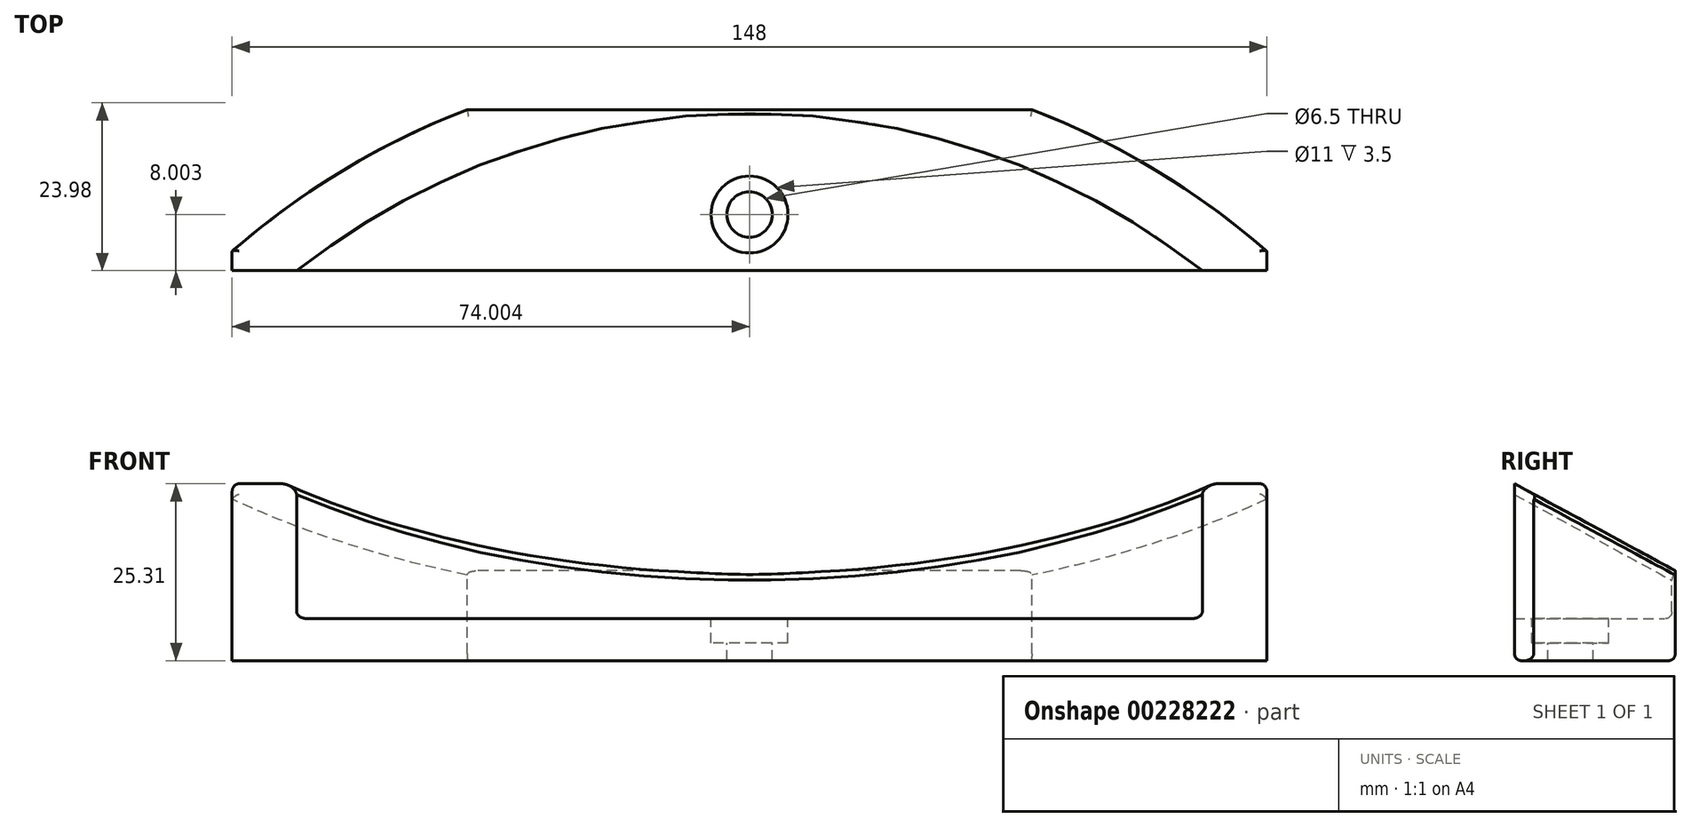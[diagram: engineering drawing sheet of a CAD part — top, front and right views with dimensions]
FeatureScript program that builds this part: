
annotation { "Feature Type Name" : "Feature", "Feature Type Description" : "" }
export const myFeature = defineFeature(function(context is Context, id is Id, definition is map)
    precondition{}
    {
        {
            var Q0;
            Q0=qCreatedBy(makeId("Top.planeOp"),FACE);
            var sketch = newSketch(context, id + "F0", { "sketchPlane" : qUnion([Q0])});
            skLineSegment(sketch, "E0.bottom", {"start": v(-72.48, -7.14) * mm, "end": v(107.52, -7.14) * mm});
            skLineSegment(sketch, "E0.top", {"start": v(-72.48, -30.14) * mm, "end": v(107.52, -30.14) * mm});
            skLineSegment(sketch, "E0.left", {"start": v(-72.48, -7.14) * mm, "end": v(-72.48, -30.14) * mm});
            skLineSegment(sketch, "E0.right", {"start": v(107.52, -7.14) * mm, "end": v(107.52, -30.14) * mm});
            skPoint(sketch, "E1", {"position": v(-64.48, -22.14) * mm});
            skPoint(sketch, "E2", {"position": v(99.52, -22.14) * mm});
            skSolve(sketch);
        }
        {
            var Q0;
            Q0=makeQuery(id+"F0.imprint","IMPRINT",FACE,{"disambiguationData":[TD([[makeQuery(id+"F0.imprint","IMPRINT",EDGE,{"derivedFrom":sQuery(id+"F0.wireOp",EDGE,"E0.bottom")}),-1.0]])]});
            extrude(context, id + "F1", {"entities" : qUnion([Q0]), "depth" : 6 * mm});
        }
        {
            var Q0;
            Q0=makeQuery(id+"F1.opExtrude","CAP_FACE",FACE,{"disambiguationData":[OSD([sQuery(id+"F0.wireOp",EDGE,"E0.bottom"),sQuery(id+"F0.wireOp",EDGE,"E0.top"),sQuery(id+"F0.wireOp",EDGE,"E0.left"),sQuery(id+"F0.wireOp",EDGE,"E0.right")])],"isStart":false});
            var sketch = newSketch(context, id + "F2", { "sketchPlane" : qUnion([Q0])});
            skPoint(sketch, "E3", {"position": v(-64.48, -22.14) * mm});
            skPoint(sketch, "E4", {"position": v(99.52, -22.14) * mm});
            skLineSegment(sketch, "E5.bottom", {"start": v(-56.48, -7.14) * mm, "end": v(91.52, -7.14) * mm});
            skLineSegment(sketch, "E5.top", {"start": v(-56.48, -30.14) * mm, "end": v(91.52, -30.14) * mm});
            skLineSegment(sketch, "E5.left", {"start": v(-56.48, -7.14) * mm, "end": v(-56.48, -30.14) * mm});
            skLineSegment(sketch, "E5.right", {"start": v(91.52, -7.14) * mm, "end": v(91.52, -30.14) * mm});
            skSolve(sketch);
        }
        {
            var Q0;
            Q0=makeQuery(id+"F2.imprint","IMPRINT",FACE,{"disambiguationData":[TD([[makeQuery(id+"F2.imprint","IMPRINT",EDGE,{"derivedFrom":sQuery(id+"F2.wireOp",EDGE,"E5.bottom")}),-1.0]])]});
            extrude(context, id + "F3", {"entities" : qUnion([Q0]), "operationType" : NewBodyOperationType.ADD, "depth" : 21 * mm});
        }
        {
            var Q0;
            Q0=makeQuery(id+"F3.opExtrude","CAP_FACE",FACE,{"disambiguationData":[OSD([sQuery(id+"F2.wireOp",EDGE,"E5.bottom"),sQuery(id+"F2.wireOp",EDGE,"E5.top"),sQuery(id+"F2.wireOp",EDGE,"E5.left"),sQuery(id+"F2.wireOp",EDGE,"E5.right")])],"isStart":false});
            var sketch = newSketch(context, id + "F4", { "sketchPlane" : qUnion([Q0])});
            skPoint(sketch, "E6", {"position": v(17.52, 2.86) * mm});
            skCircle(sketch, "E7", {"center": v(17.52, -112.14) * mm, "radius": 112.5 * mm});
            skCircle(sketch, "E8", {"center": v(17.52, -112.14) * mm, "radius": 104.5 * mm});
            skSolve(sketch);
        }
        {
            var Q0;
            {var subQ0=sQuery(id+"F4.wireOp",EDGE,"E8");var subQ1=makeQuery(id+"F3.opExtrude","CAP_EDGE",EDGE,{"disambiguationData":[OSD([sQuery(id+"F2.wireOp",EDGE,"E5.top")])],"isStart":false});var subQ2=makeQuery(id+"F4.imprint","INTERSECT",VERTEX,{"disambiguationData":[OD(0.0)],"derivedFrom":[subQ1,subQ0]});Q0=makeQuery(id+"F4.imprint","IMPRINT",FACE,{"disambiguationData":[TD([[makeQuery(id+"F4.imprint","IMPRINT",EDGE,{"disambiguationData":[TD([[subQ2,1.0]])],"derivedFrom":subQ0}),1.0]])]});}
            extrude(context, id + "F5", {"entities" : qUnion([Q0]), "operationType" : NewBodyOperationType.REMOVE, "oppositeDirection" : true, "depth" : 21 * mm});
        }
        {
            var Q0;
            {var subQ0=sQuery(id+"F4.wireOp",EDGE,"E7");var subQ1=makeQuery(id+"F3.opExtrude","CAP_EDGE",EDGE,{"disambiguationData":[OSD([sQuery(id+"F2.wireOp",EDGE,"E5.bottom")])],"isStart":false});var subQ2=makeQuery(id+"F4.imprint","INTERSECT",VERTEX,{"disambiguationData":[OD(1.0)],"derivedFrom":[subQ1,subQ0]});Q0=makeQuery(id+"F4.imprint","IMPRINT",FACE,{"disambiguationData":[TD([[makeQuery(id+"F4.imprint","IMPRINT",EDGE,{"disambiguationData":[TD([[subQ2,-1.0]])],"derivedFrom":subQ0}),-1.0]])]});}
            var Q1;
            {var subQ0=sQuery(id+"F4.wireOp",EDGE,"E7");var subQ1=makeQuery(id+"F3.opExtrude","CAP_EDGE",EDGE,{"disambiguationData":[OSD([sQuery(id+"F2.wireOp",EDGE,"E5.bottom")])],"isStart":false});var subQ2=makeQuery(id+"F4.imprint","INTERSECT",VERTEX,{"disambiguationData":[OD(0.0)],"derivedFrom":[subQ1,subQ0]});Q1=makeQuery(id+"F4.imprint","IMPRINT",FACE,{"disambiguationData":[TD([[makeQuery(id+"F4.imprint","IMPRINT",EDGE,{"disambiguationData":[TD([[subQ2,1.0]])],"derivedFrom":subQ0}),-1.0]])]});}
            extrude(context, id + "F6", {"entities" : qUnion([Q0, Q1]), "operationType" : NewBodyOperationType.REMOVE, "oppositeDirection" : true, "depth" : 35 * mm});
        }
        {
            var Q0;
            Q0=makeQuery(id+"F1.opExtrude","SWEPT_FACE",FACE,{"disambiguationData":[OSD([sQuery(id+"F0.wireOp",EDGE,"E0.right")])]});
            var sketch = newSketch(context, id + "F7", { "sketchPlane" : qUnion([Q0])});
            skLineSegment(sketch, "E9", {"start": v(-33.26, 27) * mm, "end": v(-1.82, 10) * mm});
            skLineSegment(sketch, "E10", {"start": v(-1.82, 10) * mm, "end": v(-1.82, 27.27) * mm});
            skLineSegment(sketch, "E11", {"start": v(-1.82, 27.27) * mm, "end": v(-33.26, 27) * mm});
            skSolve(sketch);
        }
        {
            var Q0;
            Q0=makeQuery(id+"F7.imprint","IMPRINT",FACE,{"disambiguationData":[TD([[makeQuery(id+"F7.imprint","IMPRINT",EDGE,{"derivedFrom":sQuery(id+"F7.wireOp",EDGE,"E9")}),1.0]])]});
            extrude(context, id + "F8", {"entities" : qUnion([Q0]), "operationType" : NewBodyOperationType.REMOVE, "oppositeDirection" : true, "depth" : 200 * mm});
        }
        {
            var Q0;
            {var subQ0=sQuery(id+"F2.wireOp",EDGE,"E5.left");Q0=makeQuery(id+"F2.imprint","IMPRINT",FACE,{"disambiguationData":[TD([[makeQuery(id+"F2.imprint","IMPRINT",EDGE,{"derivedFrom":subQ0}),-1.0]])]});}
            var Q1;
            {var subQ0=sQuery(id+"F2.wireOp",EDGE,"E5.right");Q1=makeQuery(id+"F2.imprint","IMPRINT",FACE,{"disambiguationData":[TD([[makeQuery(id+"F2.imprint","IMPRINT",EDGE,{"derivedFrom":subQ0}),1.0]])]});}
            extrude(context, id + "F9", {"entities" : qUnion([Q0, Q1]), "operationType" : NewBodyOperationType.REMOVE, "oppositeDirection" : true, "depth" : 25 * mm});
        }
        {
            var Q0;
            {var subQ0=sQuery(id+"F4.wireOp",EDGE,"E8");var subQ1=makeQuery(id+"F3.opExtrude","CAP_EDGE",EDGE,{"disambiguationData":[OSD([sQuery(id+"F2.wireOp",EDGE,"E5.top")])],"isStart":false});var subQ2=makeQuery(id+"F4.imprint","INTERSECT",VERTEX,{"disambiguationData":[OD(0.0)],"derivedFrom":[subQ1,subQ0]});Q0=makeQuery(id+"F4.imprint","IMPRINT",FACE,{"disambiguationData":[TD([[makeQuery(id+"F4.imprint","IMPRINT",EDGE,{"disambiguationData":[TD([[subQ2,1.0]])],"derivedFrom":subQ0}),1.0]])]});}
            var sketch = newSketch(context, id + "F10", { "sketchPlane" : qUnion([Q0])});
            skPoint(sketch, "E12", {"position": v(17.52, -22.14) * mm});
            skSolve(sketch);
        }
        {
            var Q0;
            Q0=sQuery(id+"F10.wireOp",VERTEX,"E12");
            var Q1;
            Q1=makeQuery(id+"F1.opExtrude","SWEPT_BODY",BODY,{"disambiguationData":[OSD([sQuery(id+"F0.wireOp",EDGE,"E0.bottom"),sQuery(id+"F0.wireOp",EDGE,"E0.top"),sQuery(id+"F0.wireOp",EDGE,"E0.left"),sQuery(id+"F0.wireOp",EDGE,"E0.right")])]});
            hole(context, id + "F11", {"style" : HoleStyle.C_BORE, "endStyle" : HoleEndStyle.THROUGH, "holeDiameter" : 6.5 * mm, "cBoreDiameter" : 11 * mm, "cBoreDepth" : 3.5 * mm, "locations" : qUnion([Q0]), "scope" : qUnion([Q1]), "isTappedThrough" : true});
        }
        {
            var Q0;
            Q0=makeQuery(id+"F5.boolean.opBoolean","COPY",EDGE,{"derivedFrom":makeQuery(id+"F5.opExtrude","CAP_EDGE",EDGE,{"disambiguationData":[OSD([sQuery(id+"F2.wireOp",EDGE,"E5.bottom")])],"isStart":false})});
            var Q1;
            Q1=makeQuery(id+"F5.boolean.opBoolean","COPY",EDGE,{"derivedFrom":makeQuery(id+"F5.opExtrude","CAP_EDGE",EDGE,{"disambiguationData":[OSD([sQuery(id+"F2.wireOp",EDGE,"E5.top")])],"isStart":false})});
            var Q2;
            {var subQ0=sQuery(id+"F4.wireOp",EDGE,"E7");var subQ1=sQuery(id+"F2.wireOp",EDGE,"E5.bottom");var subQ2=makeQuery(id+"F3.opExtrude","CAP_EDGE",EDGE,{"disambiguationData":[OSD([subQ1])],"isStart":false});var subQ3=sQuery(id+"F0.wireOp",EDGE,"E0.bottom");Q2=makeQuery(id+"F6.boolean.opBoolean","SPLIT",EDGE,{"disambiguationData":[TD([makeQuery(id+"F6.opExtrude","SWEPT_FACE",FACE,{"disambiguationData":[OSD([subQ0]),TDD([makeQuery(id+"F4.imprint","IMPRINT",EDGE,{"disambiguationData":[TD([[makeQuery(id+"F4.imprint","INTERSECT",VERTEX,{"disambiguationData":[OD(0.0)],"derivedFrom":[subQ2,subQ0]}),1.0]])],"derivedFrom":subQ0})])]})])],"derivedFrom":makeQuery(id+"F1.opExtrude","CAP_EDGE",EDGE,{"disambiguationData":[OSD([subQ3])],"isStart":true})});}
            var Q3;
            Q3=makeQuery(id+"F1.opExtrude","CAP_EDGE",EDGE,{"disambiguationData":[OSD([sQuery(id+"F0.wireOp",EDGE,"E0.top")])],"isStart":true});
            var Q4;
            {var subQ0=sQuery(id+"F4.wireOp",EDGE,"E7");var subQ1=sQuery(id+"F2.wireOp",EDGE,"E5.bottom");var subQ2=sQuery(id+"F2.wireOp",EDGE,"E5.left");var subQ6=sQuery(id+"F0.wireOp",EDGE,"E0.right");var subQ7=sQuery(id+"F0.wireOp",EDGE,"E0.left");var subQ8=sQuery(id+"F0.wireOp",EDGE,"E0.top");var subQ9=sQuery(id+"F0.wireOp",EDGE,"E0.bottom");var subQ11=makeQuery(id+"F6.opExtrude","SWEPT_EDGE",EDGE,{"disambiguationData":[OSD([subQ2,subQ0])]});Q4=makeQuery(id+"F9.boolean.opBoolean","MERGE",EDGE,{"derivedFrom":[makeQuery(id+"F6.boolean.opBoolean","COPY",EDGE,{"disambiguationData":[TD([makeQuery(id+"F1.opExtrude","CAP_FACE",FACE,{"disambiguationData":[OSD([subQ9,subQ8,subQ7,subQ6])],"isStart":true})])],"derivedFrom":subQ11}),makeQuery(id+"F6.boolean.opBoolean","COPY",EDGE,{"disambiguationData":[TD([makeQuery(id+"F3.opExtrude","CAP_FACE",FACE,{"disambiguationData":[OSD([subQ1,sQuery(id+"F2.wireOp",EDGE,"E5.top"),subQ2,sQuery(id+"F2.wireOp",EDGE,"E5.right")])],"isStart":false})])],"derivedFrom":subQ11})]});}
            var Q5;
            {var subQ0=sQuery(id+"F4.wireOp",EDGE,"E7");var subQ1=sQuery(id+"F2.wireOp",EDGE,"E5.bottom");Q5=makeQuery(id+"F6.boolean.opBoolean","COPY",EDGE,{"derivedFrom":makeQuery(id+"F6.opExtrude","SWEPT_EDGE",EDGE,{"disambiguationData":[OSD([subQ1,subQ0]),TDD([makeQuery(id+"F4.imprint","INTERSECT",VERTEX,{"disambiguationData":[OD(1.0)],"derivedFrom":[makeQuery(id+"F3.opExtrude","CAP_EDGE",EDGE,{"disambiguationData":[OSD([subQ1])],"isStart":false}),subQ0]})])]})});}
            var Q6;
            {var subQ0=sQuery(id+"F4.wireOp",EDGE,"E7");var subQ1=sQuery(id+"F2.wireOp",EDGE,"E5.bottom");var subQ2=sQuery(id+"F2.wireOp",EDGE,"E5.right");var subQ5=sQuery(id+"F0.wireOp",EDGE,"E0.right");var subQ6=sQuery(id+"F0.wireOp",EDGE,"E0.left");var subQ7=sQuery(id+"F0.wireOp",EDGE,"E0.top");var subQ8=sQuery(id+"F0.wireOp",EDGE,"E0.bottom");var subQ11=makeQuery(id+"F6.opExtrude","SWEPT_EDGE",EDGE,{"disambiguationData":[OSD([subQ2,subQ0])]});Q6=makeQuery(id+"F9.boolean.opBoolean","MERGE",EDGE,{"derivedFrom":[makeQuery(id+"F6.boolean.opBoolean","COPY",EDGE,{"disambiguationData":[TD([makeQuery(id+"F1.opExtrude","CAP_FACE",FACE,{"disambiguationData":[OSD([subQ8,subQ7,subQ6,subQ5])],"isStart":true})])],"derivedFrom":subQ11}),makeQuery(id+"F6.boolean.opBoolean","COPY",EDGE,{"disambiguationData":[TD([makeQuery(id+"F3.opExtrude","CAP_FACE",FACE,{"disambiguationData":[OSD([subQ1,sQuery(id+"F2.wireOp",EDGE,"E5.top"),sQuery(id+"F2.wireOp",EDGE,"E5.left"),subQ2])],"isStart":false})])],"derivedFrom":subQ11})]});}
            var Q7;
            {var subQ0=sQuery(id+"F4.wireOp",EDGE,"E8");Q7=makeQuery(id+"F8.boolean.opBoolean","INTERSECT",EDGE,{"derivedFrom":[makeQuery(id+"F5.boolean.opBoolean","COPY",FACE,{"derivedFrom":makeQuery(id+"F5.opExtrude","SWEPT_FACE",FACE,{"disambiguationData":[OSD([subQ0]),TDD([makeQuery(id+"F4.imprint","IMPRINT",EDGE,{"disambiguationData":[TD([[makeQuery(id+"F4.imprint","INTERSECT",VERTEX,{"disambiguationData":[OD(0.0)],"derivedFrom":[makeQuery(id+"F3.opExtrude","CAP_EDGE",EDGE,{"disambiguationData":[OSD([sQuery(id+"F2.wireOp",EDGE,"E5.bottom")])],"isStart":false}),subQ0]}),1.0]])],"derivedFrom":subQ0})])]})}),makeQuery(id+"F8.opExtrude","SWEPT_FACE",FACE,{"disambiguationData":[OSD([sQuery(id+"F7.wireOp",EDGE,"E9")])]})]});}
            var Q8;
            {var subQ0=sQuery(id+"F4.wireOp",EDGE,"E7");Q8=makeQuery(id+"F8.boolean.opBoolean","INTERSECT",EDGE,{"derivedFrom":[makeQuery(id+"F6.boolean.opBoolean","COPY",FACE,{"derivedFrom":makeQuery(id+"F6.opExtrude","SWEPT_FACE",FACE,{"disambiguationData":[OSD([subQ0]),TDD([makeQuery(id+"F4.imprint","IMPRINT",EDGE,{"disambiguationData":[TD([[makeQuery(id+"F4.imprint","INTERSECT",VERTEX,{"disambiguationData":[OD(0.0)],"derivedFrom":[makeQuery(id+"F3.opExtrude","CAP_EDGE",EDGE,{"disambiguationData":[OSD([sQuery(id+"F2.wireOp",EDGE,"E5.bottom")])],"isStart":false}),subQ0]}),1.0]])],"derivedFrom":subQ0})])]})}),makeQuery(id+"F8.opExtrude","SWEPT_FACE",FACE,{"disambiguationData":[OSD([sQuery(id+"F7.wireOp",EDGE,"E9")])]})]});}
            var Q9;
            {var subQ0=sQuery(id+"F4.wireOp",EDGE,"E8");var subQ4=sQuery(id+"F2.wireOp",EDGE,"E5.bottom");var subQ5=makeQuery(id+"F3.opExtrude","CAP_EDGE",EDGE,{"disambiguationData":[OSD([subQ4])],"isStart":false});var subQ9=sQuery(id+"F0.wireOp",EDGE,"E0.bottom");Q9=makeQuery(id+"F8.boolean.opBoolean","INTERSECT",EDGE,{"disambiguationData":[OD(0.0)],"derivedFrom":[makeQuery(id+"F6.boolean.opBoolean","SPLIT",FACE,{"disambiguationData":[TD([makeQuery(id+"F5.boolean.opBoolean","COPY",FACE,{"derivedFrom":makeQuery(id+"F5.opExtrude","SWEPT_FACE",FACE,{"disambiguationData":[OSD([subQ0]),TDD([makeQuery(id+"F4.imprint","IMPRINT",EDGE,{"disambiguationData":[TD([[makeQuery(id+"F4.imprint","INTERSECT",VERTEX,{"disambiguationData":[OD(0.0)],"derivedFrom":[subQ5,subQ0]}),1.0]])],"derivedFrom":subQ0})])]})})])],"derivedFrom":makeQuery(id+"F3.boolean.opBoolean","MERGE",FACE,{"derivedFrom":[makeQuery(id+"F1.opExtrude","SWEPT_FACE",FACE,{"disambiguationData":[OSD([subQ9])]}),makeQuery(id+"F3.opExtrude","SWEPT_FACE",FACE,{"disambiguationData":[OSD([subQ4])]})]})}),makeQuery(id+"F8.opExtrude","SWEPT_FACE",FACE,{"disambiguationData":[OSD([sQuery(id+"F7.wireOp",EDGE,"E9")])]})]});}
            var Q10;
            Q10=makeQuery(id+"F8.boolean.opBoolean","INTERSECT",EDGE,{"derivedFrom":[makeQuery(id+"F3.opExtrude","SWEPT_FACE",FACE,{"disambiguationData":[OSD([sQuery(id+"F2.wireOp",EDGE,"E5.right")])]}),makeQuery(id+"F8.opExtrude","SWEPT_FACE",FACE,{"disambiguationData":[OSD([sQuery(id+"F7.wireOp",EDGE,"E9")])]})]});
            var Q11;
            {var subQ0=sQuery(id+"F4.wireOp",EDGE,"E7");Q11=makeQuery(id+"F8.boolean.opBoolean","INTERSECT",EDGE,{"derivedFrom":[makeQuery(id+"F6.boolean.opBoolean","COPY",FACE,{"derivedFrom":makeQuery(id+"F6.opExtrude","SWEPT_FACE",FACE,{"disambiguationData":[OSD([subQ0]),TDD([makeQuery(id+"F4.imprint","IMPRINT",EDGE,{"disambiguationData":[TD([[makeQuery(id+"F4.imprint","INTERSECT",VERTEX,{"disambiguationData":[OD(1.0)],"derivedFrom":[makeQuery(id+"F3.opExtrude","CAP_EDGE",EDGE,{"disambiguationData":[OSD([sQuery(id+"F2.wireOp",EDGE,"E5.bottom")])],"isStart":false}),subQ0]}),-1.0]])],"derivedFrom":subQ0})])]})}),makeQuery(id+"F8.opExtrude","SWEPT_FACE",FACE,{"disambiguationData":[OSD([sQuery(id+"F7.wireOp",EDGE,"E9")])]})]});}
            var Q12;
            {var subQ0=sQuery(id+"F4.wireOp",EDGE,"E8");var subQ4=sQuery(id+"F2.wireOp",EDGE,"E5.bottom");var subQ5=makeQuery(id+"F3.opExtrude","CAP_EDGE",EDGE,{"disambiguationData":[OSD([subQ4])],"isStart":false});var subQ9=sQuery(id+"F0.wireOp",EDGE,"E0.bottom");Q12=makeQuery(id+"F8.boolean.opBoolean","INTERSECT",EDGE,{"disambiguationData":[OD(1.0)],"derivedFrom":[makeQuery(id+"F6.boolean.opBoolean","SPLIT",FACE,{"disambiguationData":[TD([makeQuery(id+"F5.boolean.opBoolean","COPY",FACE,{"derivedFrom":makeQuery(id+"F5.opExtrude","SWEPT_FACE",FACE,{"disambiguationData":[OSD([subQ0]),TDD([makeQuery(id+"F4.imprint","IMPRINT",EDGE,{"disambiguationData":[TD([[makeQuery(id+"F4.imprint","INTERSECT",VERTEX,{"disambiguationData":[OD(0.0)],"derivedFrom":[subQ5,subQ0]}),1.0]])],"derivedFrom":subQ0})])]})})])],"derivedFrom":makeQuery(id+"F3.boolean.opBoolean","MERGE",FACE,{"derivedFrom":[makeQuery(id+"F1.opExtrude","SWEPT_FACE",FACE,{"disambiguationData":[OSD([subQ9])]}),makeQuery(id+"F3.opExtrude","SWEPT_FACE",FACE,{"disambiguationData":[OSD([subQ4])]})]})}),makeQuery(id+"F8.opExtrude","SWEPT_FACE",FACE,{"disambiguationData":[OSD([sQuery(id+"F7.wireOp",EDGE,"E9")])]})]});}
            var Q13;
            Q13=makeQuery(id+"F8.boolean.opBoolean","INTERSECT",EDGE,{"derivedFrom":[makeQuery(id+"F3.opExtrude","SWEPT_FACE",FACE,{"disambiguationData":[OSD([sQuery(id+"F2.wireOp",EDGE,"E5.left")])]}),makeQuery(id+"F8.opExtrude","SWEPT_FACE",FACE,{"disambiguationData":[OSD([sQuery(id+"F7.wireOp",EDGE,"E9")])]})]});
            var Q14;
            {var subQ0=sQuery(id+"F4.wireOp",EDGE,"E8");var subQ1=sQuery(id+"F2.wireOp",EDGE,"E5.bottom");Q14=makeQuery(id+"F5.boolean.opBoolean","COPY",EDGE,{"derivedFrom":makeQuery(id+"F5.opExtrude","SWEPT_EDGE",EDGE,{"disambiguationData":[OSD([subQ1,subQ0]),TDD([makeQuery(id+"F4.imprint","INTERSECT",VERTEX,{"disambiguationData":[OD(0.0)],"derivedFrom":[makeQuery(id+"F3.opExtrude","CAP_EDGE",EDGE,{"disambiguationData":[OSD([subQ1])],"isStart":false}),subQ0]})])]})});}
            var Q15;
            {var subQ0=sQuery(id+"F4.wireOp",EDGE,"E8");var subQ1=sQuery(id+"F2.wireOp",EDGE,"E5.bottom");Q15=makeQuery(id+"F5.boolean.opBoolean","COPY",EDGE,{"derivedFrom":makeQuery(id+"F5.opExtrude","SWEPT_EDGE",EDGE,{"disambiguationData":[OSD([subQ1,subQ0]),TDD([makeQuery(id+"F4.imprint","INTERSECT",VERTEX,{"disambiguationData":[OD(1.0)],"derivedFrom":[makeQuery(id+"F3.opExtrude","CAP_EDGE",EDGE,{"disambiguationData":[OSD([subQ1])],"isStart":false}),subQ0]})])]})});}
            var Q16;
            {var subQ0=sQuery(id+"F4.wireOp",EDGE,"E8");Q16=makeQuery(id+"F5.boolean.opBoolean","COPY",EDGE,{"derivedFrom":makeQuery(id+"F5.opExtrude","CAP_EDGE",EDGE,{"disambiguationData":[OSD([subQ0]),TDD([makeQuery(id+"F4.imprint","IMPRINT",EDGE,{"disambiguationData":[TD([[makeQuery(id+"F4.imprint","INTERSECT",VERTEX,{"disambiguationData":[OD(0.0)],"derivedFrom":[makeQuery(id+"F3.opExtrude","CAP_EDGE",EDGE,{"disambiguationData":[OSD([sQuery(id+"F2.wireOp",EDGE,"E5.bottom")])],"isStart":false}),subQ0]}),1.0]])],"derivedFrom":subQ0})])],"isStart":false})});}
            var Q17;
            {var subQ0=sQuery(id+"F4.wireOp",EDGE,"E8");Q17=makeQuery(id+"F5.boolean.opBoolean","COPY",EDGE,{"derivedFrom":makeQuery(id+"F5.opExtrude","CAP_EDGE",EDGE,{"disambiguationData":[OSD([subQ0]),TDD([makeQuery(id+"F4.imprint","IMPRINT",EDGE,{"disambiguationData":[TD([[makeQuery(id+"F4.imprint","INTERSECT",VERTEX,{"disambiguationData":[OD(1.0)],"derivedFrom":[makeQuery(id+"F3.opExtrude","CAP_EDGE",EDGE,{"disambiguationData":[OSD([sQuery(id+"F2.wireOp",EDGE,"E5.bottom")])],"isStart":false}),subQ0]}),-1.0]])],"derivedFrom":subQ0})])],"isStart":false})});}
            var Q18;
            {var subQ0=sQuery(id+"F4.wireOp",EDGE,"E7");var subQ1=sQuery(id+"F2.wireOp",EDGE,"E5.bottom");Q18=makeQuery(id+"F6.boolean.opBoolean","COPY",EDGE,{"derivedFrom":makeQuery(id+"F6.opExtrude","SWEPT_EDGE",EDGE,{"disambiguationData":[OSD([subQ1,subQ0]),TDD([makeQuery(id+"F4.imprint","INTERSECT",VERTEX,{"disambiguationData":[OD(0.0)],"derivedFrom":[makeQuery(id+"F3.opExtrude","CAP_EDGE",EDGE,{"disambiguationData":[OSD([subQ1])],"isStart":false}),subQ0]})])]})});}
            var Q19;
            Q19=makeQuery(id+"F11.hole-0.boolean.opBoolean","COPY",EDGE,{"derivedFrom":makeQuery(id+"F11.hole-0.opRevolve","SWEPT_EDGE",EDGE,{"disambiguationData":[OSD([sQuery(id+"F11.hole-0.sketch.wireOp",EDGE,"cbore_start_line_1"),sQuery(id+"F11.hole-0.sketch.wireOp",EDGE,"core_line_2")])]})});
            var Q20;
            Q20=makeQuery(id+"F11.hole-0.boolean.opBoolean","COPY",EDGE,{"derivedFrom":makeQuery(id+"F11.hole-0.opRevolve","SWEPT_EDGE",EDGE,{"disambiguationData":[OSD([sQuery(id+"F11.hole-0.sketch.wireOp",EDGE,"cbore_start_line_2"),sQuery(id+"F11.hole-0.sketch.wireOp",EDGE,"cbore_start_line_3")])]})});
            var Q21;
            {var subQ0=sQuery(id+"F4.wireOp",EDGE,"E7");Q21=makeQuery(id+"F6.boolean.opBoolean","INTERSECT",EDGE,{"derivedFrom":[makeQuery(id+"F1.opExtrude","CAP_FACE",FACE,{"disambiguationData":[OSD([sQuery(id+"F0.wireOp",EDGE,"E0.bottom"),sQuery(id+"F0.wireOp",EDGE,"E0.top"),sQuery(id+"F0.wireOp",EDGE,"E0.left"),sQuery(id+"F0.wireOp",EDGE,"E0.right")])],"isStart":true}),makeQuery(id+"F6.opExtrude","SWEPT_FACE",FACE,{"disambiguationData":[OSD([subQ0]),TDD([makeQuery(id+"F4.imprint","IMPRINT",EDGE,{"disambiguationData":[TD([[makeQuery(id+"F4.imprint","INTERSECT",VERTEX,{"disambiguationData":[OD(0.0)],"derivedFrom":[makeQuery(id+"F3.opExtrude","CAP_EDGE",EDGE,{"disambiguationData":[OSD([sQuery(id+"F2.wireOp",EDGE,"E5.bottom")])],"isStart":false}),subQ0]}),1.0]])],"derivedFrom":subQ0})])]})]});}
            var Q22;
            {var subQ0=sQuery(id+"F4.wireOp",EDGE,"E7");Q22=makeQuery(id+"F6.boolean.opBoolean","INTERSECT",EDGE,{"derivedFrom":[makeQuery(id+"F1.opExtrude","CAP_FACE",FACE,{"disambiguationData":[OSD([sQuery(id+"F0.wireOp",EDGE,"E0.bottom"),sQuery(id+"F0.wireOp",EDGE,"E0.top"),sQuery(id+"F0.wireOp",EDGE,"E0.left"),sQuery(id+"F0.wireOp",EDGE,"E0.right")])],"isStart":true}),makeQuery(id+"F6.opExtrude","SWEPT_FACE",FACE,{"disambiguationData":[OSD([subQ0]),TDD([makeQuery(id+"F4.imprint","IMPRINT",EDGE,{"disambiguationData":[TD([[makeQuery(id+"F4.imprint","INTERSECT",VERTEX,{"disambiguationData":[OD(1.0)],"derivedFrom":[makeQuery(id+"F3.opExtrude","CAP_EDGE",EDGE,{"disambiguationData":[OSD([sQuery(id+"F2.wireOp",EDGE,"E5.bottom")])],"isStart":false}),subQ0]}),-1.0]])],"derivedFrom":subQ0})])]})]});}
            var Q23;
            Q23=makeQuery(id+"F11.hole-0.boolean.opBoolean","INTERSECT",EDGE,{"derivedFrom":[makeQuery(id+"F5.boolean.opBoolean","COPY",FACE,{"derivedFrom":makeQuery(id+"F5.opExtrude","CAP_FACE",FACE,{"disambiguationData":[OSD([sQuery(id+"F2.wireOp",EDGE,"E5.top"),sQuery(id+"F4.wireOp",EDGE,"E8")])],"isStart":false})}),makeQuery(id+"F11.hole-0.opRevolve","SWEPT_FACE",FACE,{"disambiguationData":[OSD([sQuery(id+"F11.hole-0.sketch.wireOp",EDGE,"cbore_start_line_2")])]})]});
            fillet(context, id + "F12", {"entities" : qUnion([Q0, Q1, Q2, Q3, Q4, Q5, Q6, Q7, Q8, Q9, Q10, Q11, Q12, Q13, Q14, Q15, Q16, Q17, Q18, Q19, Q20, Q21, Q22, Q23]), "radius" : 1 * mm, "tangentPropagation" : true, "allowEdgeOverflow" : false});
        }
    });
